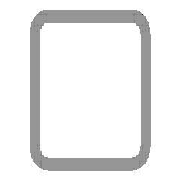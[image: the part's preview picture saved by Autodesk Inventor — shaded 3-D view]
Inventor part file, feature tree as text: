
AUTODESK INVENTOR PART (.ipt)
format: ipt  version: 2025.1 (Build 291241020, 241B)  size: 144,896 bytes
history: native  units: mm (DEFAULTED — no unit token found)
features: other x4, sketch x1, plane x1
ambient origin geometry x8: Origin, YZ Plane, XZ Plane, XY Plane, X Axis, Y Axis, Z Axis, Center Point
bodies: Solid1 (feature_tree), Body (feature_tree)
feature tree (6):
  parser-record x1  (decoder bookkeeping rows leaked as tree rows — omitted from the tree; the rows remain in map.json)
  other  "Driven Length"
  other  "Start plane"
  other  "End plane"
  sketch  "Sketch3"  dims[d3=550.0mm d4=0.0mm d7=6.0mm d9=100.0mm d11=100.0mm d12=3.0mm d13=100.0mm d14=650.0mm d15=50.0mm d16=50.0mm d17=90.0deg d18=550.0mm]
  plane  "Work Plane3"
